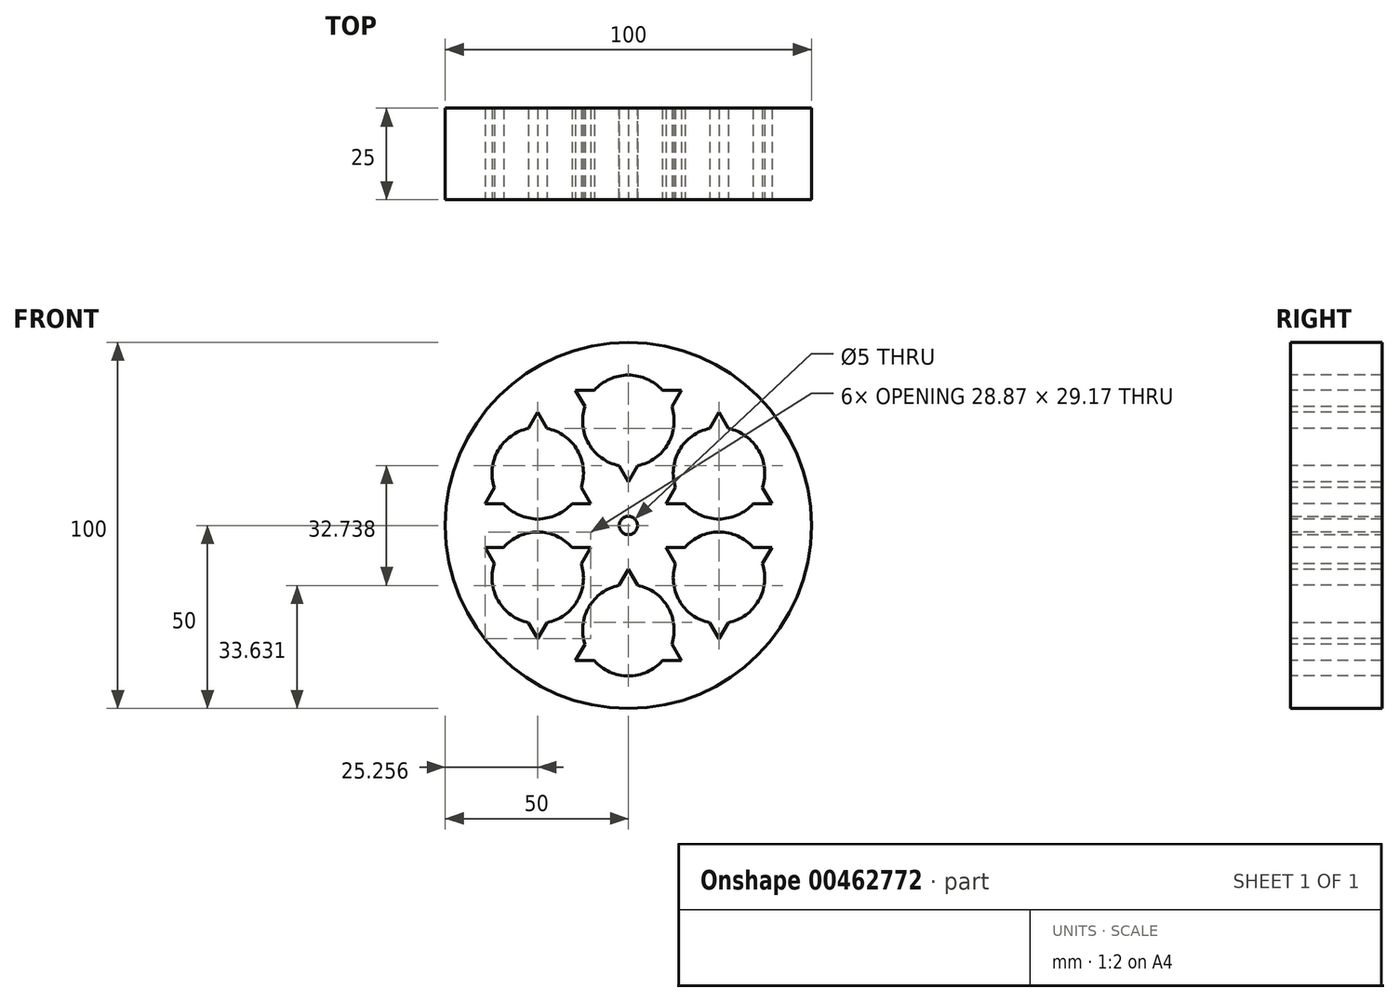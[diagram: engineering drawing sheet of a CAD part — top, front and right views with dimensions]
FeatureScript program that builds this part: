
annotation { "Feature Type Name" : "Feature", "Feature Type Description" : "" }
export const myFeature = defineFeature(function(context is Context, id is Id, definition is map)
    precondition{}
    {
        {
            var Q0;
            Q0=qCreatedBy(makeId("Front.planeOp"),FACE);
            var sketch = newSketch(context, id + "F0", { "sketchPlane" : qUnion([Q0])});
            skCircle(sketch, "E0", {"center": v(0, 0) * mm, "radius": 50 * mm});
            skCircle(sketch, "E1", {"center": v(0, 0) * mm, "radius": 2.5 * mm});
            skSolve(sketch);
        }
        {
            var Q0;
            Q0=qSketchRegion(id+"F0",true);
            extrude(context, id + "F1", {"entities" : qUnion([Q0]), "depth" : 25 * mm});
        }
        {
            var Q0;
            Q0=makeQuery(id+"F1.opExtrude","CAP_FACE",FACE,{"disambiguationData":[OSD([sQuery(id+"F0.wireOp",EDGE,"E0"),sQuery(id+"F0.wireOp",EDGE,"E1")])],"isStart":false});
            var sketch = newSketch(context, id + "F2", { "sketchPlane" : qUnion([Q0])});
            skCircle(sketch, "E2.cCircle", {"center": v(0, 28.57) * mm, "radius": 8.33 * mm, "construction": true});
            skLineSegment(sketch, "E2.0", {"start": v(14.43, 36.9) * mm, "end": v(0, 11.9) * mm});
            skLineSegment(sketch, "E2.1", {"start": v(0, 11.9) * mm, "end": v(-14.43, 36.9) * mm});
            skLineSegment(sketch, "E2.2", {"start": v(-14.43, 36.9) * mm, "end": v(14.43, 36.9) * mm});
            skPoint(sketch, "E2.0.midPoint", {"position": v(7.22, 24.4) * mm});
            skLineSegment(sketch, "E3", {"start": v(0, 0) * mm, "end": v(77.64, 0) * mm, "construction": true});
            skPoint(sketch, "E4.center", {"position": v(0, 0) * mm});
            skLineSegment(sketch, "E5", {"start": v(0, 0) * mm, "end": v(0, 56.69) * mm, "construction": true});
            skCircle(sketch, "E6.cCircle", {"center": v(24.74, 14.29) * mm, "radius": 8.33 * mm, "construction": true});
            skLineSegment(sketch, "E6.0", {"start": v(24.74, 30.95) * mm, "end": v(39.18, 5.95) * mm});
            skLineSegment(sketch, "E6.1", {"start": v(39.18, 5.95) * mm, "end": v(10.3, 5.95) * mm});
            skLineSegment(sketch, "E6.2", {"start": v(10.3, 5.95) * mm, "end": v(24.74, 30.95) * mm});
            skPoint(sketch, "E6.0.midPoint", {"position": v(31.96, 18.45) * mm});
            skLineSegment(sketch, "E7", {"start": v(10.3, 5.95) * mm, "end": v(36.54, 21.1) * mm, "construction": true});
            skLineSegment(sketch, "E8.1.0", {"start": v(-39.18, 5.95) * mm, "end": v(-24.74, 30.95) * mm});
            skLineSegment(sketch, "E8.1.1", {"start": v(-10.3, 5.95) * mm, "end": v(-39.18, 5.95) * mm});
            skLineSegment(sketch, "E8.1.2", {"start": v(-24.74, 30.95) * mm, "end": v(-10.3, 5.95) * mm});
            skLineSegment(sketch, "E8.1.3", {"start": v(-10.3, -5.95) * mm, "end": v(-24.74, -30.95) * mm});
            skLineSegment(sketch, "E8.1.4", {"start": v(-24.74, -30.95) * mm, "end": v(-39.18, -5.95) * mm});
            skLineSegment(sketch, "E8.1.5", {"start": v(-39.18, -5.95) * mm, "end": v(-10.3, -5.95) * mm});
            skLineSegment(sketch, "E8.2.0", {"start": v(14.43, -36.9) * mm, "end": v(-14.43, -36.9) * mm});
            skLineSegment(sketch, "E8.2.1", {"start": v(0, -11.9) * mm, "end": v(14.43, -36.9) * mm});
            skLineSegment(sketch, "E8.2.2", {"start": v(-14.43, -36.9) * mm, "end": v(0, -11.9) * mm});
            skLineSegment(sketch, "E8.2.3", {"start": v(10.3, -5.95) * mm, "end": v(39.18, -5.95) * mm});
            skLineSegment(sketch, "E8.2.4", {"start": v(39.18, -5.95) * mm, "end": v(24.74, -30.95) * mm});
            skLineSegment(sketch, "E8.2.5", {"start": v(24.74, -30.95) * mm, "end": v(10.3, -5.95) * mm});
            skCircle(sketch, "E9", {"center": v(0, 28.57) * mm, "radius": 12.5 * mm});
            skCircle(sketch, "E10", {"center": v(24.74, 14.29) * mm, "radius": 12.5 * mm});
            skCircle(sketch, "E11.1.0", {"center": v(-24.74, -14.29) * mm, "radius": 12.5 * mm});
            skCircle(sketch, "E11.1.1", {"center": v(-24.74, 14.29) * mm, "radius": 12.5 * mm});
            skCircle(sketch, "E11.2.0", {"center": v(24.74, -14.29) * mm, "radius": 12.5 * mm});
            skCircle(sketch, "E11.2.1", {"center": v(0, -28.57) * mm, "radius": 12.5 * mm});
            skSolve(sketch);
        }
        {
            var Q0;
            Q0=qSketchRegion(id+"F2",true);
            extrude(context, id + "F3", {"entities" : qUnion([Q0]), "operationType" : NewBodyOperationType.REMOVE, "oppositeDirection" : true, "depth" : 25 * mm});
        }
        {
            var Q0;
            {var subQ0=sQuery(id+"F2.wireOp",EDGE,"E2.2");var subQ1=sQuery(id+"F2.wireOp",EDGE,"E2.0");var subQ2=makeQuery(id+"F2.imprint","INTERSECT",VERTEX,{"derivedFrom":[subQ1,subQ0]});Q0=makeQuery(id+"F2.imprint","IMPRINT",FACE,{"disambiguationData":[TD([[makeQuery(id+"F2.imprint","IMPRINT",EDGE,{"disambiguationData":[TD([[subQ2,-1.0]])],"derivedFrom":subQ1}),-1.0]])]});}
            var Q1;
            {var subQ0=sQuery(id+"F2.wireOp",EDGE,"E9");var subQ1=sQuery(id+"F2.wireOp",EDGE,"E2.0");var subQ2=makeQuery(id+"F2.imprint","INTERSECT",VERTEX,{"disambiguationData":[OD(0.0)],"derivedFrom":[subQ1,subQ0]});Q1=makeQuery(id+"F2.imprint","IMPRINT",FACE,{"disambiguationData":[TD([[makeQuery(id+"F2.imprint","IMPRINT",EDGE,{"disambiguationData":[TD([[subQ2,-1.0]])],"derivedFrom":subQ1}),1.0]])]});}
            var Q2;
            {var subQ0=sQuery(id+"F2.wireOp",EDGE,"E2.1");var subQ1=sQuery(id+"F2.wireOp",EDGE,"E2.0");var subQ2=makeQuery(id+"F2.imprint","INTERSECT",VERTEX,{"derivedFrom":[subQ1,subQ0]});Q2=makeQuery(id+"F2.imprint","IMPRINT",FACE,{"disambiguationData":[TD([[makeQuery(id+"F2.imprint","IMPRINT",EDGE,{"disambiguationData":[TD([[subQ2,1.0]])],"derivedFrom":subQ1}),-1.0]])]});}
            var Q3;
            {var subQ0=sQuery(id+"F2.wireOp",EDGE,"E9");var subQ1=sQuery(id+"F2.wireOp",EDGE,"E2.1");var subQ2=makeQuery(id+"F2.imprint","INTERSECT",VERTEX,{"disambiguationData":[OD(0.0)],"derivedFrom":[subQ1,subQ0]});Q3=makeQuery(id+"F2.imprint","IMPRINT",FACE,{"disambiguationData":[TD([[makeQuery(id+"F2.imprint","IMPRINT",EDGE,{"disambiguationData":[TD([[subQ2,-1.0]])],"derivedFrom":subQ1}),1.0]])]});}
            var Q4;
            {var subQ0=sQuery(id+"F2.wireOp",EDGE,"E2.2");var subQ1=sQuery(id+"F2.wireOp",EDGE,"E2.1");var subQ2=makeQuery(id+"F2.imprint","INTERSECT",VERTEX,{"derivedFrom":[subQ1,subQ0]});Q4=makeQuery(id+"F2.imprint","IMPRINT",FACE,{"disambiguationData":[TD([[makeQuery(id+"F2.imprint","IMPRINT",EDGE,{"disambiguationData":[TD([[subQ2,1.0]])],"derivedFrom":subQ1}),-1.0]])]});}
            var Q5;
            {var subQ0=sQuery(id+"F2.wireOp",EDGE,"E9");var subQ1=sQuery(id+"F2.wireOp",EDGE,"E2.2");var subQ2=makeQuery(id+"F2.imprint","INTERSECT",VERTEX,{"disambiguationData":[OD(0.0)],"derivedFrom":[subQ1,subQ0]});Q5=makeQuery(id+"F2.imprint","IMPRINT",FACE,{"disambiguationData":[TD([[makeQuery(id+"F2.imprint","IMPRINT",EDGE,{"disambiguationData":[TD([[subQ2,-1.0]])],"derivedFrom":subQ1}),1.0]])]});}
            var Q6;
            {var subQ0=sQuery(id+"F2.wireOp",EDGE,"E6.2");var subQ1=sQuery(id+"F2.wireOp",EDGE,"E6.0");var subQ2=makeQuery(id+"F2.imprint","INTERSECT",VERTEX,{"derivedFrom":[subQ1,subQ0]});Q6=makeQuery(id+"F2.imprint","IMPRINT",FACE,{"disambiguationData":[TD([[makeQuery(id+"F2.imprint","IMPRINT",EDGE,{"disambiguationData":[TD([[subQ2,-1.0]])],"derivedFrom":subQ1}),-1.0]])]});}
            var Q7;
            {var subQ0=sQuery(id+"F2.wireOp",EDGE,"E10");var subQ1=sQuery(id+"F2.wireOp",EDGE,"E6.0");var subQ2=makeQuery(id+"F2.imprint","INTERSECT",VERTEX,{"disambiguationData":[OD(0.0)],"derivedFrom":[subQ1,subQ0]});Q7=makeQuery(id+"F2.imprint","IMPRINT",FACE,{"disambiguationData":[TD([[makeQuery(id+"F2.imprint","IMPRINT",EDGE,{"disambiguationData":[TD([[subQ2,-1.0]])],"derivedFrom":subQ1}),1.0]])]});}
            var Q8;
            {var subQ0=sQuery(id+"F2.wireOp",EDGE,"E6.1");var subQ1=sQuery(id+"F2.wireOp",EDGE,"E6.0");var subQ2=makeQuery(id+"F2.imprint","INTERSECT",VERTEX,{"derivedFrom":[subQ1,subQ0]});Q8=makeQuery(id+"F2.imprint","IMPRINT",FACE,{"disambiguationData":[TD([[makeQuery(id+"F2.imprint","IMPRINT",EDGE,{"disambiguationData":[TD([[subQ2,1.0]])],"derivedFrom":subQ1}),-1.0]])]});}
            var Q9;
            {var subQ0=sQuery(id+"F2.wireOp",EDGE,"E10");var subQ1=sQuery(id+"F2.wireOp",EDGE,"E6.1");var subQ2=makeQuery(id+"F2.imprint","INTERSECT",VERTEX,{"disambiguationData":[OD(0.0)],"derivedFrom":[subQ1,subQ0]});Q9=makeQuery(id+"F2.imprint","IMPRINT",FACE,{"disambiguationData":[TD([[makeQuery(id+"F2.imprint","IMPRINT",EDGE,{"disambiguationData":[TD([[subQ2,-1.0]])],"derivedFrom":subQ1}),1.0]])]});}
            var Q10;
            {var subQ0=sQuery(id+"F2.wireOp",EDGE,"E6.2");var subQ1=sQuery(id+"F2.wireOp",EDGE,"E6.1");var subQ2=makeQuery(id+"F2.imprint","INTERSECT",VERTEX,{"derivedFrom":[subQ1,subQ0]});Q10=makeQuery(id+"F2.imprint","IMPRINT",FACE,{"disambiguationData":[TD([[makeQuery(id+"F2.imprint","IMPRINT",EDGE,{"disambiguationData":[TD([[subQ2,1.0]])],"derivedFrom":subQ1}),-1.0]])]});}
            var Q11;
            {var subQ0=sQuery(id+"F2.wireOp",EDGE,"E10");var subQ1=sQuery(id+"F2.wireOp",EDGE,"E6.2");var subQ2=makeQuery(id+"F2.imprint","INTERSECT",VERTEX,{"disambiguationData":[OD(0.0)],"derivedFrom":[subQ1,subQ0]});Q11=makeQuery(id+"F2.imprint","IMPRINT",FACE,{"disambiguationData":[TD([[makeQuery(id+"F2.imprint","IMPRINT",EDGE,{"disambiguationData":[TD([[subQ2,-1.0]])],"derivedFrom":subQ1}),1.0]])]});}
            var Q12;
            {var subQ0=sQuery(id+"F2.wireOp",EDGE,"E8.1.5");var subQ1=sQuery(id+"F2.wireOp",EDGE,"E8.1.3");var subQ2=makeQuery(id+"F2.imprint","INTERSECT",VERTEX,{"derivedFrom":[subQ1,subQ0]});Q12=makeQuery(id+"F2.imprint","IMPRINT",FACE,{"disambiguationData":[TD([[makeQuery(id+"F2.imprint","IMPRINT",EDGE,{"disambiguationData":[TD([[subQ2,-1.0]])],"derivedFrom":subQ1}),-1.0]])]});}
            var Q13;
            {var subQ0=sQuery(id+"F2.wireOp",EDGE,"E11.1.0");var subQ1=sQuery(id+"F2.wireOp",EDGE,"E8.1.3");var subQ2=makeQuery(id+"F2.imprint","INTERSECT",VERTEX,{"disambiguationData":[OD(0.0)],"derivedFrom":[subQ1,subQ0]});Q13=makeQuery(id+"F2.imprint","IMPRINT",FACE,{"disambiguationData":[TD([[makeQuery(id+"F2.imprint","IMPRINT",EDGE,{"disambiguationData":[TD([[subQ2,-1.0]])],"derivedFrom":subQ1}),1.0]])]});}
            var Q14;
            {var subQ0=sQuery(id+"F2.wireOp",EDGE,"E8.1.4");var subQ1=sQuery(id+"F2.wireOp",EDGE,"E8.1.3");var subQ2=makeQuery(id+"F2.imprint","INTERSECT",VERTEX,{"derivedFrom":[subQ1,subQ0]});Q14=makeQuery(id+"F2.imprint","IMPRINT",FACE,{"disambiguationData":[TD([[makeQuery(id+"F2.imprint","IMPRINT",EDGE,{"disambiguationData":[TD([[subQ2,1.0]])],"derivedFrom":subQ1}),-1.0]])]});}
            var Q15;
            {var subQ0=sQuery(id+"F2.wireOp",EDGE,"E11.1.0");var subQ1=sQuery(id+"F2.wireOp",EDGE,"E8.1.4");var subQ2=makeQuery(id+"F2.imprint","INTERSECT",VERTEX,{"disambiguationData":[OD(0.0)],"derivedFrom":[subQ1,subQ0]});Q15=makeQuery(id+"F2.imprint","IMPRINT",FACE,{"disambiguationData":[TD([[makeQuery(id+"F2.imprint","IMPRINT",EDGE,{"disambiguationData":[TD([[subQ2,-1.0]])],"derivedFrom":subQ1}),1.0]])]});}
            var Q16;
            {var subQ0=sQuery(id+"F2.wireOp",EDGE,"E8.1.5");var subQ1=sQuery(id+"F2.wireOp",EDGE,"E8.1.4");var subQ2=makeQuery(id+"F2.imprint","INTERSECT",VERTEX,{"derivedFrom":[subQ1,subQ0]});Q16=makeQuery(id+"F2.imprint","IMPRINT",FACE,{"disambiguationData":[TD([[makeQuery(id+"F2.imprint","IMPRINT",EDGE,{"disambiguationData":[TD([[subQ2,1.0]])],"derivedFrom":subQ1}),-1.0]])]});}
            var Q17;
            {var subQ0=sQuery(id+"F2.wireOp",EDGE,"E11.1.0");var subQ1=sQuery(id+"F2.wireOp",EDGE,"E8.1.5");var subQ2=makeQuery(id+"F2.imprint","INTERSECT",VERTEX,{"disambiguationData":[OD(0.0)],"derivedFrom":[subQ1,subQ0]});Q17=makeQuery(id+"F2.imprint","IMPRINT",FACE,{"disambiguationData":[TD([[makeQuery(id+"F2.imprint","IMPRINT",EDGE,{"disambiguationData":[TD([[subQ2,-1.0]])],"derivedFrom":subQ1}),1.0]])]});}
            var Q18;
            {var subQ0=sQuery(id+"F2.wireOp",EDGE,"E8.2.1");var subQ1=sQuery(id+"F2.wireOp",EDGE,"E8.2.0");var subQ2=makeQuery(id+"F2.imprint","INTERSECT",VERTEX,{"derivedFrom":[subQ1,subQ0]});Q18=makeQuery(id+"F2.imprint","IMPRINT",FACE,{"disambiguationData":[TD([[makeQuery(id+"F2.imprint","IMPRINT",EDGE,{"disambiguationData":[TD([[subQ2,-1.0]])],"derivedFrom":subQ1}),-1.0]])]});}
            var Q19;
            {var subQ0=sQuery(id+"F2.wireOp",EDGE,"E11.2.1");var subQ1=sQuery(id+"F2.wireOp",EDGE,"E8.2.0");var subQ2=makeQuery(id+"F2.imprint","INTERSECT",VERTEX,{"disambiguationData":[OD(0.0)],"derivedFrom":[subQ1,subQ0]});Q19=makeQuery(id+"F2.imprint","IMPRINT",FACE,{"disambiguationData":[TD([[makeQuery(id+"F2.imprint","IMPRINT",EDGE,{"disambiguationData":[TD([[subQ2,-1.0]])],"derivedFrom":subQ1}),1.0]])]});}
            var Q20;
            {var subQ0=sQuery(id+"F2.wireOp",EDGE,"E8.2.2");var subQ1=sQuery(id+"F2.wireOp",EDGE,"E8.2.0");var subQ2=makeQuery(id+"F2.imprint","INTERSECT",VERTEX,{"derivedFrom":[subQ1,subQ0]});Q20=makeQuery(id+"F2.imprint","IMPRINT",FACE,{"disambiguationData":[TD([[makeQuery(id+"F2.imprint","IMPRINT",EDGE,{"disambiguationData":[TD([[subQ2,1.0]])],"derivedFrom":subQ1}),-1.0]])]});}
            var Q21;
            {var subQ0=sQuery(id+"F2.wireOp",EDGE,"E8.2.2");var subQ1=sQuery(id+"F2.wireOp",EDGE,"E8.2.1");var subQ2=makeQuery(id+"F2.imprint","INTERSECT",VERTEX,{"derivedFrom":[subQ1,subQ0]});Q21=makeQuery(id+"F2.imprint","IMPRINT",FACE,{"disambiguationData":[TD([[makeQuery(id+"F2.imprint","IMPRINT",EDGE,{"disambiguationData":[TD([[subQ2,-1.0]])],"derivedFrom":subQ1}),-1.0]])]});}
            var Q22;
            {var subQ0=sQuery(id+"F2.wireOp",EDGE,"E11.2.1");var subQ1=sQuery(id+"F2.wireOp",EDGE,"E8.2.1");var subQ2=makeQuery(id+"F2.imprint","INTERSECT",VERTEX,{"disambiguationData":[OD(0.0)],"derivedFrom":[subQ1,subQ0]});Q22=makeQuery(id+"F2.imprint","IMPRINT",FACE,{"disambiguationData":[TD([[makeQuery(id+"F2.imprint","IMPRINT",EDGE,{"disambiguationData":[TD([[subQ2,-1.0]])],"derivedFrom":subQ1}),1.0]])]});}
            var Q23;
            {var subQ0=sQuery(id+"F2.wireOp",EDGE,"E11.2.1");var subQ1=sQuery(id+"F2.wireOp",EDGE,"E8.2.2");var subQ2=makeQuery(id+"F2.imprint","INTERSECT",VERTEX,{"disambiguationData":[OD(0.0)],"derivedFrom":[subQ1,subQ0]});Q23=makeQuery(id+"F2.imprint","IMPRINT",FACE,{"disambiguationData":[TD([[makeQuery(id+"F2.imprint","IMPRINT",EDGE,{"disambiguationData":[TD([[subQ2,-1.0]])],"derivedFrom":subQ1}),1.0]])]});}
            var Q24;
            {var subQ0=sQuery(id+"F2.wireOp",EDGE,"E8.2.5");var subQ1=sQuery(id+"F2.wireOp",EDGE,"E8.2.3");var subQ2=makeQuery(id+"F2.imprint","INTERSECT",VERTEX,{"derivedFrom":[subQ1,subQ0]});Q24=makeQuery(id+"F2.imprint","IMPRINT",FACE,{"disambiguationData":[TD([[makeQuery(id+"F2.imprint","IMPRINT",EDGE,{"disambiguationData":[TD([[subQ2,-1.0]])],"derivedFrom":subQ1}),-1.0]])]});}
            var Q25;
            {var subQ0=sQuery(id+"F2.wireOp",EDGE,"E11.2.0");var subQ1=sQuery(id+"F2.wireOp",EDGE,"E8.2.3");var subQ2=makeQuery(id+"F2.imprint","INTERSECT",VERTEX,{"disambiguationData":[OD(0.0)],"derivedFrom":[subQ1,subQ0]});Q25=makeQuery(id+"F2.imprint","IMPRINT",FACE,{"disambiguationData":[TD([[makeQuery(id+"F2.imprint","IMPRINT",EDGE,{"disambiguationData":[TD([[subQ2,-1.0]])],"derivedFrom":subQ1}),1.0]])]});}
            var Q26;
            {var subQ0=sQuery(id+"F2.wireOp",EDGE,"E8.2.4");var subQ1=sQuery(id+"F2.wireOp",EDGE,"E8.2.3");var subQ2=makeQuery(id+"F2.imprint","INTERSECT",VERTEX,{"derivedFrom":[subQ1,subQ0]});Q26=makeQuery(id+"F2.imprint","IMPRINT",FACE,{"disambiguationData":[TD([[makeQuery(id+"F2.imprint","IMPRINT",EDGE,{"disambiguationData":[TD([[subQ2,1.0]])],"derivedFrom":subQ1}),-1.0]])]});}
            var Q27;
            {var subQ0=sQuery(id+"F2.wireOp",EDGE,"E11.2.0");var subQ1=sQuery(id+"F2.wireOp",EDGE,"E8.2.4");var subQ2=makeQuery(id+"F2.imprint","INTERSECT",VERTEX,{"disambiguationData":[OD(0.0)],"derivedFrom":[subQ1,subQ0]});Q27=makeQuery(id+"F2.imprint","IMPRINT",FACE,{"disambiguationData":[TD([[makeQuery(id+"F2.imprint","IMPRINT",EDGE,{"disambiguationData":[TD([[subQ2,-1.0]])],"derivedFrom":subQ1}),1.0]])]});}
            var Q28;
            {var subQ0=sQuery(id+"F2.wireOp",EDGE,"E8.2.5");var subQ1=sQuery(id+"F2.wireOp",EDGE,"E8.2.4");var subQ2=makeQuery(id+"F2.imprint","INTERSECT",VERTEX,{"derivedFrom":[subQ1,subQ0]});Q28=makeQuery(id+"F2.imprint","IMPRINT",FACE,{"disambiguationData":[TD([[makeQuery(id+"F2.imprint","IMPRINT",EDGE,{"disambiguationData":[TD([[subQ2,1.0]])],"derivedFrom":subQ1}),-1.0]])]});}
            var Q29;
            {var subQ0=sQuery(id+"F2.wireOp",EDGE,"E11.2.0");var subQ1=sQuery(id+"F2.wireOp",EDGE,"E8.2.5");var subQ2=makeQuery(id+"F2.imprint","INTERSECT",VERTEX,{"disambiguationData":[OD(0.0)],"derivedFrom":[subQ1,subQ0]});Q29=makeQuery(id+"F2.imprint","IMPRINT",FACE,{"disambiguationData":[TD([[makeQuery(id+"F2.imprint","IMPRINT",EDGE,{"disambiguationData":[TD([[subQ2,-1.0]])],"derivedFrom":subQ1}),1.0]])]});}
            var Q30;
            {var subQ0=sQuery(id+"F2.wireOp",EDGE,"E9");var subQ4=sQuery(id+"F2.wireOp",EDGE,"E2.0");var subQ5=makeQuery(id+"F2.imprint","INTERSECT",VERTEX,{"disambiguationData":[OD(0.0)],"derivedFrom":[subQ4,subQ0]});Q30=makeQuery(id+"F2.imprint","IMPRINT",FACE,{"disambiguationData":[TD([[makeQuery(id+"F2.imprint","IMPRINT",EDGE,{"disambiguationData":[TD([[subQ5,-1.0]])],"derivedFrom":subQ4}),-1.0]])]});}
            var Q31;
            {var subQ0=sQuery(id+"F2.wireOp",EDGE,"E10");var subQ4=sQuery(id+"F2.wireOp",EDGE,"E6.0");var subQ5=makeQuery(id+"F2.imprint","INTERSECT",VERTEX,{"disambiguationData":[OD(0.0)],"derivedFrom":[subQ4,subQ0]});Q31=makeQuery(id+"F2.imprint","IMPRINT",FACE,{"disambiguationData":[TD([[makeQuery(id+"F2.imprint","IMPRINT",EDGE,{"disambiguationData":[TD([[subQ5,-1.0]])],"derivedFrom":subQ4}),-1.0]])]});}
            var Q32;
            {var subQ0=sQuery(id+"F2.wireOp",EDGE,"E11.1.0");var subQ7=sQuery(id+"F2.wireOp",EDGE,"E8.1.3");var subQ8=makeQuery(id+"F2.imprint","INTERSECT",VERTEX,{"disambiguationData":[OD(0.0)],"derivedFrom":[subQ7,subQ0]});Q32=makeQuery(id+"F2.imprint","IMPRINT",FACE,{"disambiguationData":[TD([[makeQuery(id+"F2.imprint","IMPRINT",EDGE,{"disambiguationData":[TD([[subQ8,-1.0]])],"derivedFrom":subQ7}),-1.0]])]});}
            var Q33;
            {var subQ0=sQuery(id+"F2.wireOp",EDGE,"E11.2.1");var subQ1=sQuery(id+"F2.wireOp",EDGE,"E8.2.0");var subQ2=makeQuery(id+"F2.imprint","INTERSECT",VERTEX,{"disambiguationData":[OD(0.0)],"derivedFrom":[subQ1,subQ0]});Q33=makeQuery(id+"F2.imprint","IMPRINT",FACE,{"disambiguationData":[TD([[makeQuery(id+"F2.imprint","IMPRINT",EDGE,{"disambiguationData":[TD([[subQ2,-1.0]])],"derivedFrom":subQ1}),-1.0]])]});}
            var Q34;
            {var subQ0=sQuery(id+"F2.wireOp",EDGE,"E11.2.0");var subQ7=sQuery(id+"F2.wireOp",EDGE,"E8.2.3");var subQ8=makeQuery(id+"F2.imprint","INTERSECT",VERTEX,{"disambiguationData":[OD(0.0)],"derivedFrom":[subQ7,subQ0]});Q34=makeQuery(id+"F2.imprint","IMPRINT",FACE,{"disambiguationData":[TD([[makeQuery(id+"F2.imprint","IMPRINT",EDGE,{"disambiguationData":[TD([[subQ8,-1.0]])],"derivedFrom":subQ7}),-1.0]])]});}
            var Q35;
            {var subQ0=sQuery(id+"F2.wireOp",EDGE,"E8.1.2");var subQ1=sQuery(id+"F2.wireOp",EDGE,"E8.1.1");var subQ2=makeQuery(id+"F2.imprint","INTERSECT",VERTEX,{"derivedFrom":[subQ1,subQ0]});Q35=makeQuery(id+"F2.imprint","IMPRINT",FACE,{"disambiguationData":[TD([[makeQuery(id+"F2.imprint","IMPRINT",EDGE,{"disambiguationData":[TD([[subQ2,-1.0]])],"derivedFrom":subQ1}),-1.0]])]});}
            var Q36;
            {var subQ0=sQuery(id+"F2.wireOp",EDGE,"E8.1.1");var subQ1=sQuery(id+"F2.wireOp",EDGE,"E8.1.0");var subQ2=makeQuery(id+"F2.imprint","INTERSECT",VERTEX,{"derivedFrom":[subQ1,subQ0]});Q36=makeQuery(id+"F2.imprint","IMPRINT",FACE,{"disambiguationData":[TD([[makeQuery(id+"F2.imprint","IMPRINT",EDGE,{"disambiguationData":[TD([[subQ2,-1.0]])],"derivedFrom":subQ1}),-1.0]])]});}
            var Q37;
            {var subQ0=sQuery(id+"F2.wireOp",EDGE,"E11.1.1");var subQ1=sQuery(id+"F2.wireOp",EDGE,"E8.1.1");var subQ2=makeQuery(id+"F2.imprint","INTERSECT",VERTEX,{"disambiguationData":[OD(0.0)],"derivedFrom":[subQ1,subQ0]});Q37=makeQuery(id+"F2.imprint","IMPRINT",FACE,{"disambiguationData":[TD([[makeQuery(id+"F2.imprint","IMPRINT",EDGE,{"disambiguationData":[TD([[subQ2,-1.0]])],"derivedFrom":subQ1}),1.0]])]});}
            var Q38;
            {var subQ0=sQuery(id+"F2.wireOp",EDGE,"E11.1.1");var subQ1=sQuery(id+"F2.wireOp",EDGE,"E8.1.0");var subQ2=makeQuery(id+"F2.imprint","INTERSECT",VERTEX,{"disambiguationData":[OD(0.0)],"derivedFrom":[subQ1,subQ0]});Q38=makeQuery(id+"F2.imprint","IMPRINT",FACE,{"disambiguationData":[TD([[makeQuery(id+"F2.imprint","IMPRINT",EDGE,{"disambiguationData":[TD([[subQ2,-1.0]])],"derivedFrom":subQ1}),1.0]])]});}
            var Q39;
            {var subQ0=sQuery(id+"F2.wireOp",EDGE,"E11.1.1");var subQ1=sQuery(id+"F2.wireOp",EDGE,"E8.1.2");var subQ2=makeQuery(id+"F2.imprint","INTERSECT",VERTEX,{"disambiguationData":[OD(0.0)],"derivedFrom":[subQ1,subQ0]});Q39=makeQuery(id+"F2.imprint","IMPRINT",FACE,{"disambiguationData":[TD([[makeQuery(id+"F2.imprint","IMPRINT",EDGE,{"disambiguationData":[TD([[subQ2,-1.0]])],"derivedFrom":subQ1}),1.0]])]});}
            var Q40;
            {var subQ0=sQuery(id+"F2.wireOp",EDGE,"E8.1.2");var subQ1=sQuery(id+"F2.wireOp",EDGE,"E8.1.0");var subQ2=makeQuery(id+"F2.imprint","INTERSECT",VERTEX,{"derivedFrom":[subQ1,subQ0]});Q40=makeQuery(id+"F2.imprint","IMPRINT",FACE,{"disambiguationData":[TD([[makeQuery(id+"F2.imprint","IMPRINT",EDGE,{"disambiguationData":[TD([[subQ2,1.0]])],"derivedFrom":subQ1}),-1.0]])]});}
            extrude(context, id + "F4", {"entities" : qUnion([Q0, Q1, Q2, Q3, Q4, Q5, Q6, Q7, Q8, Q9, Q10, Q11, Q12, Q13, Q14, Q15, Q16, Q17, Q18, Q19, Q20, Q21, Q22, Q23, Q24, Q25, Q26, Q27, Q28, Q29, Q30, Q31, Q32, Q33, Q34, Q35, Q36, Q37, Q38, Q39, Q40]), "operationType" : NewBodyOperationType.REMOVE, "oppositeDirection" : true, "depth" : 25 * mm});
        }
    });
